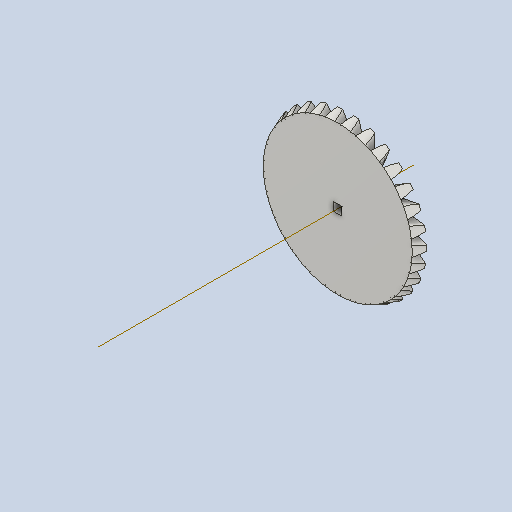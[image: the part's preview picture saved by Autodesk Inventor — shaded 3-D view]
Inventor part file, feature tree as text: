
AUTODESK INVENTOR PART (.ipt)
format: ipt  version: 2022 (Build 260153000, 153)  size: 1,464,832 bytes
history: native  units: in
note: dims shown in document units (in); Inventor stores cm internally (conversion verified against a paired STEP export)
features: other x30, sketch x3, extrude x2, chamfer x1, projected_geometry x1
ambient origin geometry x8: Origin, YZ Plane, XZ Plane, XY Plane, X Axis, Y Axis, Z Axis, Center Point
bodies: Solid1 (feature_tree)
feature tree (37):
  other  "Bevel Gear2"
  extrude  "Extrusion1"  TaperAngle=0.0deg  [1 undecoded]
  extrude  "Extrusion2"  TaperAngle=90.0deg  [1 undecoded]
  chamfer  "Chamfer1"  [1 undecoded]
  other  "Solid1::Bevel Gear2"
  other  "TaggingFeature1"
  other  "Teeth Body Sketch"
  other  "Start Sketch"
  other  "End Sketch"
  other  "End Sketch Right"
  other  "End Sketch Left"
  other  "Body Sketch"
  sketch  "Sketch6"  dims[d0=0.3937in d48=0.0in]
  other  "3D Sketch Right"
  other  "3D Sketch Left"
  other  "Mesh Plane"
  other  "Top Plane"
  other  "Mesh Plane2"
  other  "Tooth Plane"
  other  "End Plane"
  other  "End Plane Right"
  other  "End Plane Left"
  other  "Z Axis_1"
  other  "Top Point"
  other  "Start Point"
  other  "End Point"
  other  "Srf1"
  sketch  "Sketch8"  dims[d49=0.0in d50=90.0deg]
  sketch  "Sketch9"  dims[d52=0.0in d53=0.0in d54=0.0in d1=0.1309in d2=0.0in d3=0.0in d4=0.4764in d5=0.2in d6=0.0in d7=0.0472in d8=0.125in d9=45.0deg]
  projected_geometry  "Projected Loop1"
  other  "Srf1::Derived"
  other  "Start plane iMate"
  other  "Mesh iMate2"
  other  "Axis Angle iMate"
  other  "Axis iMate"
  other  "Mesh iMate"
  other  "Intersection iMate"
note: 3 required parameter values undecoded (feature->parameter linkage not recoverable at this tier; creation-order binding heuristic only, values carry confidence <= 0.55)
